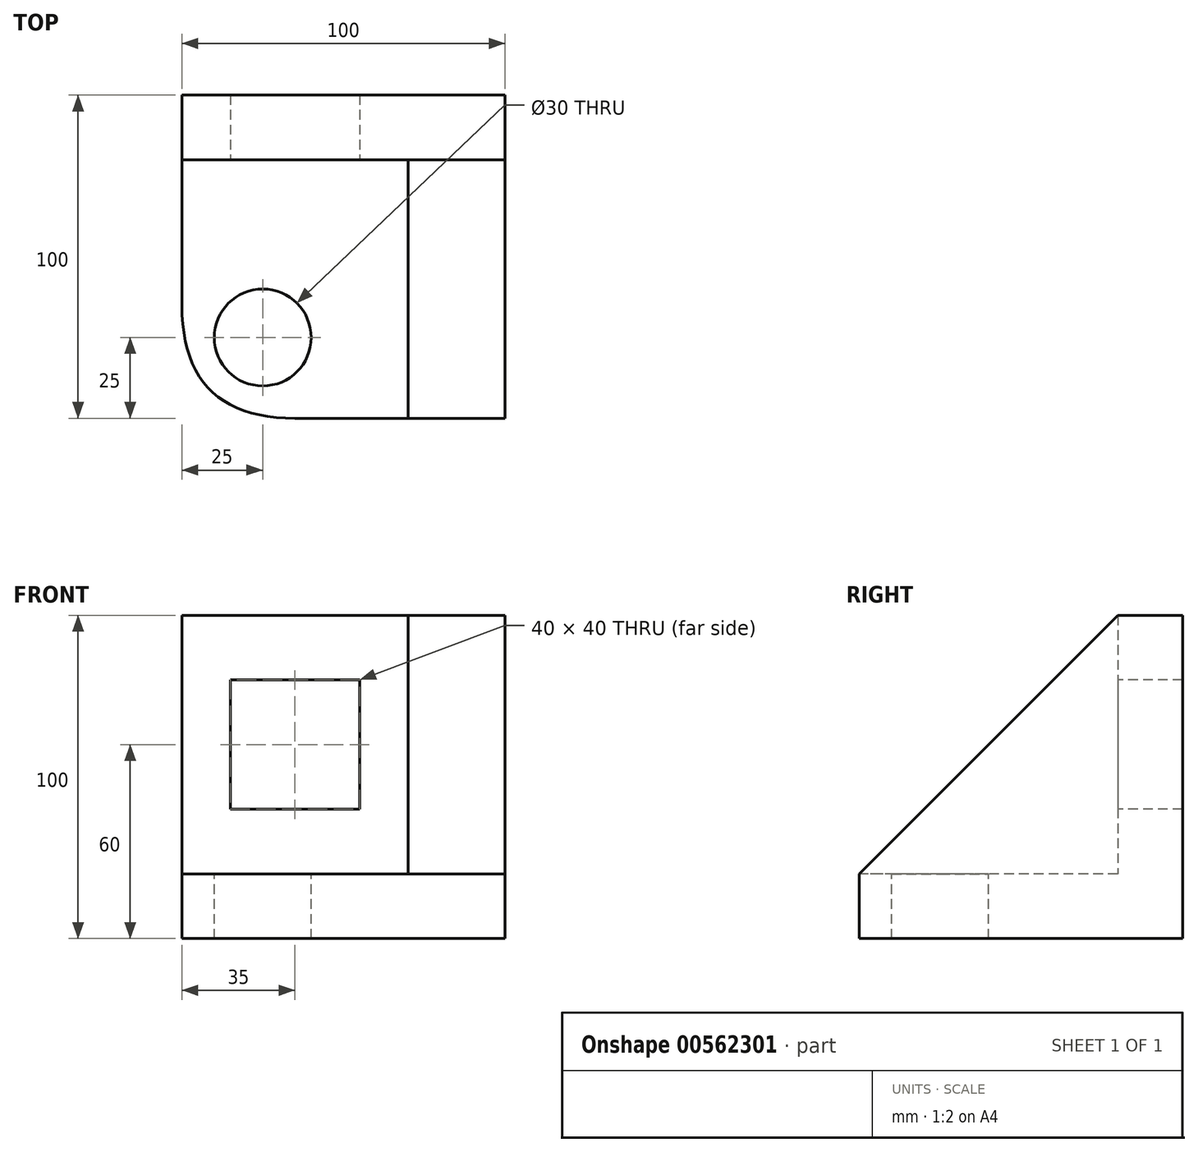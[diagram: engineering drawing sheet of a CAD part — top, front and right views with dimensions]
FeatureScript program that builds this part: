
annotation { "Feature Type Name" : "Feature", "Feature Type Description" : "" }
export const myFeature = defineFeature(function(context is Context, id is Id, definition is map)
    precondition{}
    {
        {
            var Q0;
            Q0=qCreatedBy(makeId("Top.planeOp"),FACE);
            var sketch = newSketch(context, id + "F0", { "sketchPlane" : qUnion([Q0])});
            skLineSegment(sketch, "E0.bottom", {"start": v(-50, 50) * mm, "end": v(50, 50) * mm});
            skLineSegment(sketch, "E0.top", {"start": v(-50, -50) * mm, "end": v(50, -50) * mm});
            skLineSegment(sketch, "E0.left", {"start": v(-50, 50) * mm, "end": v(-50, -50) * mm});
            skLineSegment(sketch, "E0.right", {"start": v(50, 50) * mm, "end": v(50, -50) * mm});
            skPoint(sketch, "E0.middle", {"position": v(0, 0) * mm});
            skSolve(sketch);
        }
        {
            var Q0;
            Q0=makeQuery(id+"F0.imprint","IMPRINT",FACE,{"disambiguationData":[TD([[makeQuery(id+"F0.imprint","IMPRINT",EDGE,{"derivedFrom":sQuery(id+"F0.wireOp",EDGE,"E0.bottom")}),-1.0]])]});
            extrude(context, id + "F1", {"entities" : qUnion([Q0]), "depth" : 20 * mm, "offsetDistance" : 25 * mm});
        }
        {
            var Q0;
            Q0=makeQuery(id+"F1.opExtrude","CAP_FACE",FACE,{"disambiguationData":[OSD([sQuery(id+"F0.wireOp",EDGE,"E0.bottom"),sQuery(id+"F0.wireOp",EDGE,"E0.top"),sQuery(id+"F0.wireOp",EDGE,"E0.left"),sQuery(id+"F0.wireOp",EDGE,"E0.right")])],"isStart":false});
            var sketch = newSketch(context, id + "F2", { "sketchPlane" : qUnion([Q0])});
            skLineSegment(sketch, "E1.bottom", {"start": v(-50, 50) * mm, "end": v(50, 50) * mm});
            skLineSegment(sketch, "E1.top", {"start": v(-50, 30) * mm, "end": v(50, 30) * mm});
            skLineSegment(sketch, "E1.left", {"start": v(-50, 50) * mm, "end": v(-50, 30) * mm});
            skLineSegment(sketch, "E1.right", {"start": v(50, 50) * mm, "end": v(50, 30) * mm});
            skSolve(sketch);
        }
        {
            var Q0;
            Q0=makeQuery(id+"F2.imprint","IMPRINT",FACE,{"disambiguationData":[TD([[makeQuery(id+"F2.imprint","IMPRINT",EDGE,{"derivedFrom":sQuery(id+"F2.wireOp",EDGE,"E1.bottom")}),-1.0]])]});
            extrude(context, id + "F3", {"entities" : qUnion([Q0]), "operationType" : NewBodyOperationType.ADD, "depth" : 80 * mm, "offsetDistance" : 25 * mm});
        }
        {
            var Q0;
            Q0=makeQuery(id+"F1.opExtrude","CAP_FACE",FACE,{"disambiguationData":[OSD([sQuery(id+"F0.wireOp",EDGE,"E0.bottom"),sQuery(id+"F0.wireOp",EDGE,"E0.top"),sQuery(id+"F0.wireOp",EDGE,"E0.left"),sQuery(id+"F0.wireOp",EDGE,"E0.right")])],"isStart":false});
            var sketch = newSketch(context, id + "F4", { "sketchPlane" : qUnion([Q0])});
            skPoint(sketch, "E2", {"position": v(-25, -25) * mm});
            skCircle(sketch, "E3", {"center": v(-25, -25) * mm, "radius": 15 * mm});
            skSolve(sketch);
        }
        {
            var Q0;
            Q0 = qSketchRegion(id + "F4", true);
            extrude(context, id + "F5", {"entities" : qUnion([Q0]), "operationType" : NewBodyOperationType.REMOVE, "oppositeDirection" : true, "depth" : 20 * mm, "offsetDistance" : 25 * mm});
        }
        {
            var Q0;
            Q0=makeQuery(id+"F1.opExtrude","SWEPT_EDGE",EDGE,{"disambiguationData":[OSD([sQuery(id+"F0.wireOp",EDGE,"E0.top"),sQuery(id+"F0.wireOp",EDGE,"E0.left")])]});
            fillet(context, id + "F6", {"entities" : qUnion([Q0]), "radius" : 35 * mm, "tangentPropagation" : true, "rho" : 0.5, "crossSection" : FilletCrossSection.CONIC, "allowEdgeOverflow" : false});
        }
        {
            var Q0;
            Q0=makeQuery(id+"F1.opExtrude","CAP_FACE",FACE,{"disambiguationData":[OSD([sQuery(id+"F0.wireOp",EDGE,"E0.bottom"),sQuery(id+"F0.wireOp",EDGE,"E0.top"),sQuery(id+"F0.wireOp",EDGE,"E0.left"),sQuery(id+"F0.wireOp",EDGE,"E0.right")])],"isStart":false});
            var sketch = newSketch(context, id + "F7", { "sketchPlane" : qUnion([Q0])});
            skLineSegment(sketch, "E4.bottom", {"start": v(50, 30) * mm, "end": v(20, 30) * mm});
            skLineSegment(sketch, "E4.top", {"start": v(50, -50) * mm, "end": v(20, -50) * mm});
            skLineSegment(sketch, "E4.left", {"start": v(50, 30) * mm, "end": v(50, -50) * mm});
            skLineSegment(sketch, "E4.right", {"start": v(20, 30) * mm, "end": v(20, -50) * mm});
            skSolve(sketch);
        }
        {
            var Q0;
            Q0 = qSketchRegion(id + "F7", true);
            extrude(context, id + "F8", {"entities" : qUnion([Q0]), "operationType" : NewBodyOperationType.ADD, "depth" : 80 * mm, "offsetDistance" : 25 * mm});
        }
        {
            var Q0;
            Q0=makeQuery(id+"F8.opExtrude","CAP_EDGE",EDGE,{"disambiguationData":[OSD([sQuery(id+"F7.wireOp",EDGE,"E4.top")])],"isStart":false});
            chamfer(context, id + "F9", {"entities" : qUnion([Q0]), "width" : 80 * mm, "tangentPropagation" : true});
        }
        {
            var Q0;
            Q0=makeQuery(id+"F3.opExtrude","SWEPT_FACE",FACE,{"disambiguationData":[OSD([sQuery(id+"F2.wireOp",EDGE,"E1.top")])]});
            var sketch = newSketch(context, id + "F10", { "sketchPlane" : qUnion([Q0])});
            skPoint(sketch, "E5", {"position": v(-15, 60) * mm});
            skLineSegment(sketch, "E6.bottom", {"start": v(-35, 80) * mm, "end": v(5, 80) * mm});
            skLineSegment(sketch, "E6.top", {"start": v(-35, 40) * mm, "end": v(5, 40) * mm});
            skLineSegment(sketch, "E6.left", {"start": v(-35, 80) * mm, "end": v(-35, 40) * mm});
            skLineSegment(sketch, "E6.right", {"start": v(5, 80) * mm, "end": v(5, 40) * mm});
            skSolve(sketch);
        }
        {
            var Q0;
            Q0=makeQuery(id+"F10.imprint","IMPRINT",FACE,{"disambiguationData":[TD([[makeQuery(id+"F10.imprint","IMPRINT",EDGE,{"derivedFrom":sQuery(id+"F10.wireOp",EDGE,"E6.bottom")}),-1.0]])]});
            extrude(context, id + "F11", {"entities" : qUnion([Q0]), "operationType" : NewBodyOperationType.REMOVE, "oppositeDirection" : true, "depth" : 20 * mm, "offsetDistance" : 25 * mm});
        }
    });
